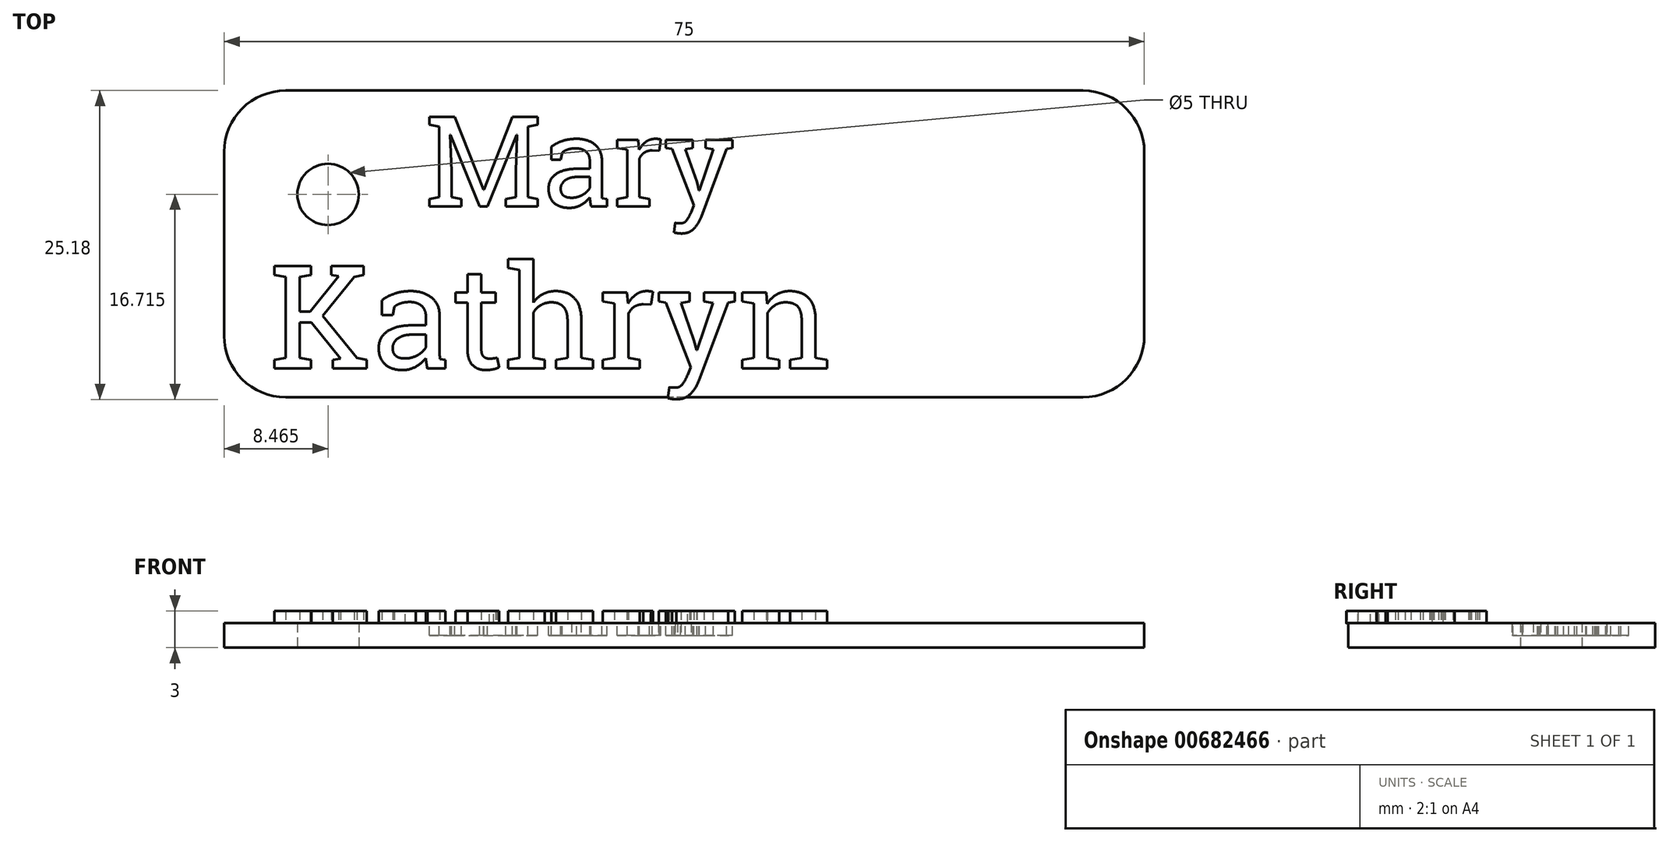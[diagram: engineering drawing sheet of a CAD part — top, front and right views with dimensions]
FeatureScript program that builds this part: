
annotation { "Feature Type Name" : "Feature", "Feature Type Description" : "" }
export const myFeature = defineFeature(function(context is Context, id is Id, definition is map)
    precondition{}
    {
        {
            var Q0;
            Q0=qCreatedBy(makeId("Top.planeOp"),FACE);
            var sketch = newSketch(context, id + "F0", { "sketchPlane" : qUnion([Q0])});
            skLineSegment(sketch, "E0.bottom", {"start": v(32.5, 12.5) * mm, "end": v(-32.5, 12.5) * mm});
            skLineSegment(sketch, "E0.top", {"start": v(32.5, -12.5) * mm, "end": v(-32.5, -12.5) * mm});
            skLineSegment(sketch, "E0.left", {"start": v(37.5, 7.5) * mm, "end": v(37.5, -7.5) * mm});
            skLineSegment(sketch, "E0.right", {"start": v(-37.5, 7.5) * mm, "end": v(-37.5, -7.5) * mm});
            skPoint(sketch, "E0.middle", {"position": v(0, 0) * mm});
            skPoint(sketch, "E1.visualSharp", {"position": v(-37.5, 12.5) * mm});
            skArc(sketch, "E1.filletArc", {"start": v(-32.5, 12.5) * mm, "mid": v(-36.04, 11.04) * mm, "end": v(-37.5, 7.5) * mm});
            skPoint(sketch, "E2.visualSharp", {"position": v(37.5, 12.5) * mm});
            skArc(sketch, "E2.filletArc", {"start": v(37.5, 7.5) * mm, "mid": v(36.04, 11.04) * mm, "end": v(32.5, 12.5) * mm});
            skPoint(sketch, "E3.visualSharp", {"position": v(37.5, -12.5) * mm});
            skArc(sketch, "E3.filletArc", {"start": v(32.5, -12.5) * mm, "mid": v(36.04, -11.04) * mm, "end": v(37.5, -7.5) * mm});
            skPoint(sketch, "E4.visualSharp", {"position": v(-37.5, -12.5) * mm});
            skArc(sketch, "E4.filletArc", {"start": v(-37.5, -7.5) * mm, "mid": v(-36.04, -11.04) * mm, "end": v(-32.5, -12.5) * mm});
            skSolve(sketch);
        }
        {
            var Q0;
            Q0 = qSketchRegion(id + "F0", true);
            extrude(context, id + "F1", {"entities" : qUnion([Q0]), "depth" : 2 * mm, "offsetDistance" : 25 * mm});
        }
        {
            var Q0;
            Q0=makeQuery(id+"F0.imprint","IMPRINT",FACE,{"disambiguationData":[TD([[makeQuery(id+"F0.imprint","IMPRINT",EDGE,{"derivedFrom":sQuery(id+"F0.wireOp",EDGE,"E0.bottom")}),1.0]])]});
            var sketch = newSketch(context, id + "F2", { "sketchPlane" : qUnion([Q0])});
            skPoint(sketch, "E5", {"position": v(-29.04, 4.04) * mm});
            skSolve(sketch);
        }
        {
            var Q0;
            Q0=sQuery(id+"F2.wireOp",VERTEX,"E5");
            var Q1;
            Q1=makeQuery(id+"F1.opExtrude","SWEPT_BODY",BODY,{"disambiguationData":[OSD([sQuery(id+"F0.wireOp",EDGE,"E0.bottom"),sQuery(id+"F0.wireOp",EDGE,"E0.top"),sQuery(id+"F0.wireOp",EDGE,"E0.left"),sQuery(id+"F0.wireOp",EDGE,"E0.right"),sQuery(id+"F0.wireOp",EDGE,"E1.filletArc"),sQuery(id+"F0.wireOp",EDGE,"E2.filletArc"),sQuery(id+"F0.wireOp",EDGE,"E3.filletArc"),sQuery(id+"F0.wireOp",EDGE,"E4.filletArc")])]});
            hole(context, id + "F3", {"style" : HoleStyle.SIMPLE, "endStyle" : HoleEndStyle.THROUGH, "oppositeDirection" : true, "holeDiameter" : 5 * mm, "majorDiameter" : 5 * mm, "isTappedThrough" : true, "tappedDepth" : 12 * mm, "tapClearance" : 3, "locations" : qUnion([Q0]), "scope" : qUnion([Q1])});
        }
        {
            var Q0;
            Q0=makeQuery(id+"F1.opExtrude","CAP_FACE",FACE,{"disambiguationData":[OSD([sQuery(id+"F0.wireOp",EDGE,"E0.bottom"),sQuery(id+"F0.wireOp",EDGE,"E0.top"),sQuery(id+"F0.wireOp",EDGE,"E0.left"),sQuery(id+"F0.wireOp",EDGE,"E0.right"),sQuery(id+"F0.wireOp",EDGE,"E1.filletArc"),sQuery(id+"F0.wireOp",EDGE,"E2.filletArc"),sQuery(id+"F0.wireOp",EDGE,"E3.filletArc"),sQuery(id+"F0.wireOp",EDGE,"E4.filletArc")])],"isStart":false});
            var sketch = newSketch(context, id + "F4", { "sketchPlane" : qUnion([Q0])});
            skText(sketch, "E6", { "text": "Mary", "fontName": "RobotoSlab-Regular.ttf"});
            const initialGuessF4  = {"E6": [-0.02114, 0.00304, 1, 0, 0.0074]};
            skSetInitialGuess(sketch, initialGuessF4);
            skSolve(sketch);
        }
        {
            var Q0;
            Q0 = qSketchRegion(id + "F4", true);
            extrude(context, id + "F5", {"entities" : qUnion([Q0]), "operationType" : NewBodyOperationType.REMOVE, "oppositeDirection" : true, "depth" : 1 * mm, "offsetDistance" : 25 * mm});
        }
        {
            var Q0;
            Q0=makeQuery(id+"F4.imprint","IMPRINT",FACE,{"disambiguationData":[TD([[makeQuery(id+"F4.imprint","IMPRINT",EDGE,{"derivedFrom":sQuery(id+"F4.wireOp",EDGE,"E6.sketch_text.stroke-0")}),1.0]])]});
            var sketch = newSketch(context, id + "F6", { "sketchPlane" : qUnion([Q0])});
            skText(sketch, "E7", { "text": "Kathryn", "fontName": "RobotoSlab-Regular.ttf"});
            const initialGuessF6  = {"E7": [-0.03383, -0.01017, 1, 0, 0.00846]};
            skSetInitialGuess(sketch, initialGuessF6);
            skSolve(sketch);
        }
        {
            var Q0;
            Q0 = qSketchRegion(id + "F6", true);
            extrude(context, id + "F7", {"entities" : qUnion([Q0]), "operationType" : NewBodyOperationType.ADD, "depth" : 1 * mm, "offsetDistance" : 25 * mm});
        }
    });
